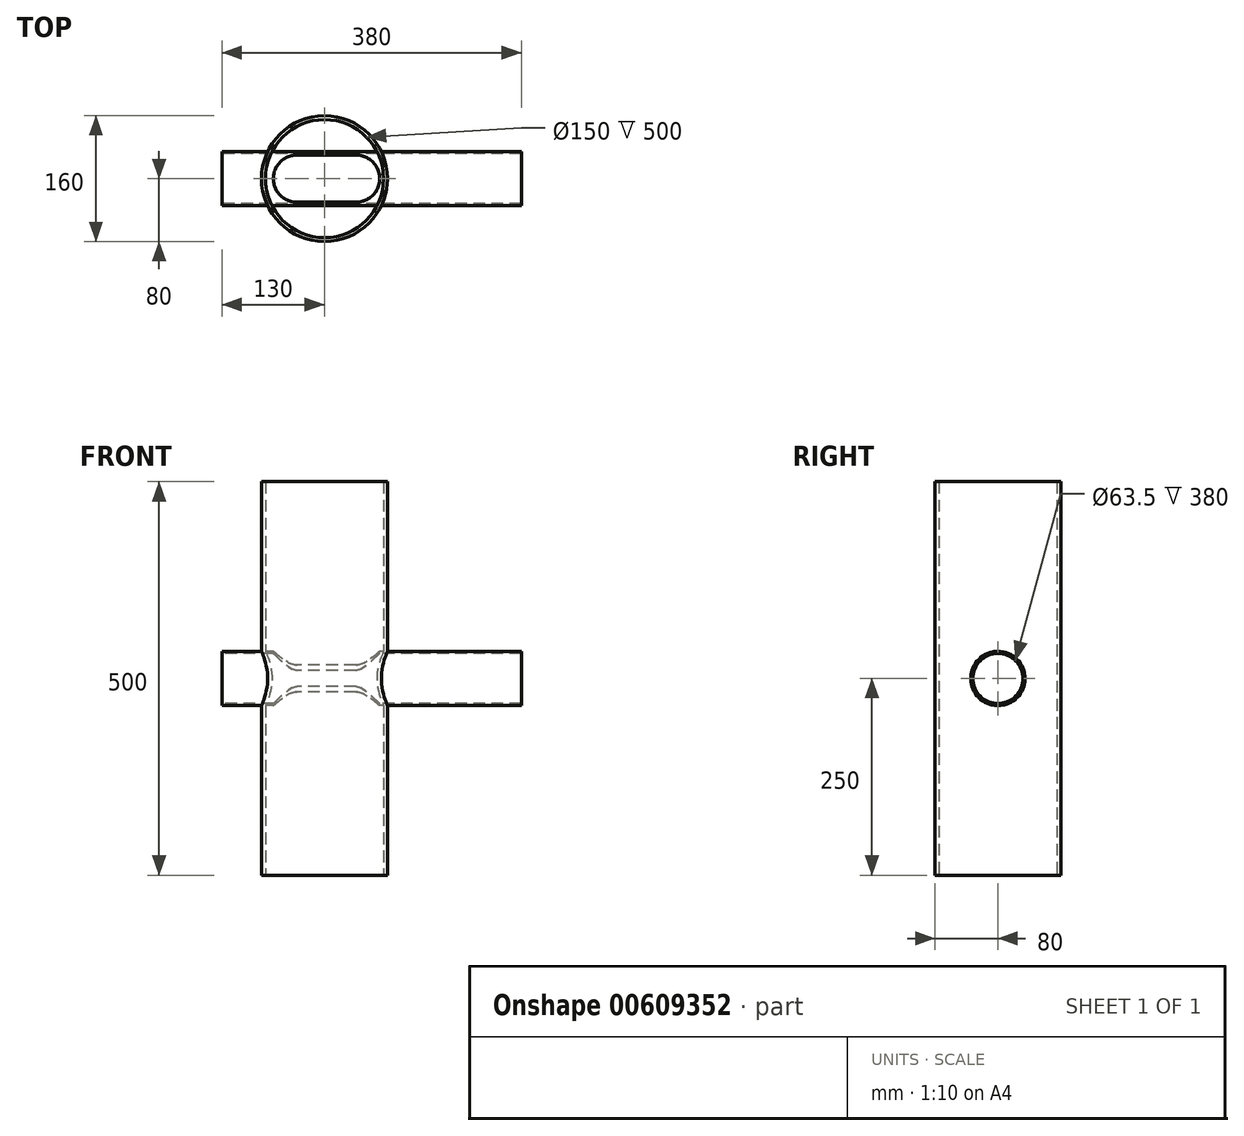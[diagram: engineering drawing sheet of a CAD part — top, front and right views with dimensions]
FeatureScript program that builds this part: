
annotation { "Feature Type Name" : "Feature", "Feature Type Description" : "" }
export const myFeature = defineFeature(function(context is Context, id is Id, definition is map)
    precondition{}
    {
        {
            var Q0;
            Q0=qCreatedBy(makeId("Top.planeOp"),FACE);
            var sketch = newSketch(context, id + "F0", { "sketchPlane" : qUnion([Q0])});
            skCircle(sketch, "E0", {"center": v(0, 0) * mm, "radius": 80 * mm});
            skCircle(sketch, "E1", {"center": v(0, 0) * mm, "radius": 75 * mm});
            skSolve(sketch);
        }
        {
            var Q0;
            Q0=makeQuery(id+"F0.imprint","IMPRINT",FACE,{"disambiguationData":[TD([[makeQuery(id+"F0.imprint","IMPRINT",EDGE,{"derivedFrom":sQuery(id+"F0.wireOp",EDGE,"E0")}),1.0]])]});
            extrude(context, id + "F1", {"entities" : qUnion([Q0]), "endBound" : BoundingType.SYMMETRIC, "depth" : 500 * mm, "offsetDistance" : 25 * mm});
        }
        {
            var Q0;
            Q0=qCreatedBy(makeId("Right.planeOp"),FACE);
            var sketch = newSketch(context, id + "F2", { "sketchPlane" : qUnion([Q0])});
            skCircle(sketch, "E2", {"center": v(0, 0) * mm, "radius": 31.75 * mm});
            skCircle(sketch, "E3", {"center": v(0, 0) * mm, "radius": 34.5 * mm});
            skSolve(sketch);
        }
        {
            var Q0;
            Q0=makeQuery(id+"F2.imprint","IMPRINT",FACE,{"disambiguationData":[TD([[makeQuery(id+"F2.imprint","IMPRINT",EDGE,{"derivedFrom":sQuery(id+"F2.wireOp",EDGE,"E2")}),-1.0]])]});
            extrude(context, id + "F3", {"entities" : qUnion([Q0]), "endBound" : BoundingType.SYMMETRIC, "depth" : 500 * mm, "offsetDistance" : 25 * mm});
        }
        {
            var Q0;
            Q0=qCreatedBy(makeId("Top.planeOp"),FACE);
            var sketch = newSketch(context, id + "F4", { "sketchPlane" : qUnion([Q0])});
            skCircle(sketch, "E4", {"center": v(0, 0) * mm, "radius": 75 * mm});
            skCircle(sketch, "E5", {"center": v(0, 0) * mm, "radius": 80 * mm});
            skSolve(sketch);
        }
        {
            var Q0;
            Q0=makeQuery(id+"F2.imprint","IMPRINT",FACE,{"disambiguationData":[TD([[makeQuery(id+"F2.imprint","IMPRINT",EDGE,{"derivedFrom":sQuery(id+"F2.wireOp",EDGE,"E2")}),1.0]])]});
            extrude(context, id + "F5", {"entities" : qUnion([Q0]), "operationType" : NewBodyOperationType.REMOVE, "endBound" : BoundingType.SYMMETRIC, "oppositeDirection" : true, "depth" : 500 * mm, "offsetDistance" : 25 * mm});
        }
        {
            var Q0;
            Q0=qCreatedBy(makeId("Top.planeOp"),FACE);
            var sketch = newSketch(context, id + "F6", { "sketchPlane" : qUnion([Q0])});
            skArc(sketch, "E6", {"start": v(-35.05, 19.92) * mm, "mid": v(-55.05, -0.08) * mm, "end": v(-35.05, -20.08) * mm});
            skArc(sketch, "E7", {"start": v(39.34, -20.08) * mm, "mid": v(59.34, -0.08) * mm, "end": v(39.34, 19.92) * mm});
            skLineSegment(sketch, "E8", {"start": v(-35.05, 19.92) * mm, "end": v(39.34, 19.92) * mm});
            skLineSegment(sketch, "E9", {"start": v(-35.05, -20.08) * mm, "end": v(39.34, -20.08) * mm});
            skSolve(sketch);
        }
        {
            var Q0;
            Q0=makeQuery(id+"F6.imprint","IMPRINT",FACE,{"disambiguationData":[TD([[makeQuery(id+"F6.imprint","IMPRINT",EDGE,{"derivedFrom":sQuery(id+"F6.wireOp",EDGE,"E6")}),1.0]])]});
            extrude(context, id + "F7", {"entities" : qUnion([Q0]), "endBound" : BoundingType.SYMMETRIC, "depth" : 100 * mm, "offsetDistance" : 25 * mm});
        }
        {
            var Q0;
            Q0=makeQuery(id+"F7.opExtrude","CAP_FACE",FACE,{"disambiguationData":[OSD([sQuery(id+"F6.wireOp",EDGE,"E6"),sQuery(id+"F6.wireOp",EDGE,"E7"),sQuery(id+"F6.wireOp",EDGE,"E8"),sQuery(id+"F6.wireOp",EDGE,"E9")])],"isStart":false});
            var sketch = newSketch(context, id + "F8", { "sketchPlane" : qUnion([Q0])});
            skLineSegment(sketch, "E10", {"start": v(-35.05, 19.92) * mm, "end": v(-35.05, -20.08) * mm});
            skLineSegment(sketch, "E11", {"start": v(39.34, 19.92) * mm, "end": v(39.34, -20.08) * mm});
            skSolve(sketch);
        }
        {
            var Q0;
            Q0=makeQuery(id+"F8.imprint","IMPRINT",FACE,{"disambiguationData":[TD([[makeQuery(id+"F8.imprint","IMPRINT",EDGE,{"derivedFrom":sQuery(id+"F8.wireOp",EDGE,"E10")}),1.0]])]});
            var sketch = newSketch(context, id + "F9", { "sketchPlane" : qUnion([Q0])});
            skArc(sketch, "E12", {"start": v(-35.02, 30) * mm, "mid": v(-65.02, 0) * mm, "end": v(-35.02, -30) * mm});
            skArc(sketch, "E13", {"start": v(39.98, -30) * mm, "mid": v(69.98, 0) * mm, "end": v(39.98, 30) * mm});
            skLineSegment(sketch, "E14", {"start": v(-35.02, 30) * mm, "end": v(39.98, 30) * mm});
            skLineSegment(sketch, "E15", {"start": v(39.98, -30) * mm, "end": v(-35.02, -30) * mm});
            skSolve(sketch);
        }
        {
            var Q0;
            Q0 = qSketchRegion(id + "F9", true);
            extrude(context, id + "F10", {"entities" : qUnion([Q0]), "operationType" : NewBodyOperationType.REMOVE, "oppositeDirection" : true, "depth" : 200 * mm, "offsetDistance" : 25 * mm});
        }
        {
            var Q0;
            Q0=qCreatedBy(makeId("Top.planeOp"),FACE);
            var sketch = newSketch(context, id + "F11", { "sketchPlane" : qUnion([Q0])});
            skSolve(sketch);
        }
        {
            var Q0;
            Q0 = qSketchRegion(id + "F11", true);
            var Q1;
            Q1=makeQuery(id+"F0.imprint","IMPRINT",FACE,{"disambiguationData":[TD([[makeQuery(id+"F0.imprint","IMPRINT",EDGE,{"derivedFrom":sQuery(id+"F0.wireOp",EDGE,"E0")}),1.0]])]});
            extrude(context, id + "F12", {"entities" : qUnion([Q0, Q1]), "operationType" : NewBodyOperationType.ADD, "endBound" : BoundingType.SYMMETRIC, "depth" : 500 * mm, "offsetDistance" : 25 * mm});
        }
        {
            var Q0;
            Q0=qCreatedBy(makeId("Right.planeOp"),FACE);
            var sketch = newSketch(context, id + "F13", { "sketchPlane" : qUnion([Q0])});
            skCircle(sketch, "E16", {"center": v(0, 0) * mm, "radius": 31.75 * mm});
            skSolve(sketch);
        }
        {
            var Q0;
            Q0 = qSketchRegion(id + "F13", true);
            var Q1;
            Q1=makeQuery(id+"F2.imprint","IMPRINT",FACE,{"disambiguationData":[TD([[makeQuery(id+"F2.imprint","IMPRINT",EDGE,{"derivedFrom":sQuery(id+"F2.wireOp",EDGE,"E2")}),1.0]])]});
            extrude(context, id + "F14", {"entities" : qUnion([Q0, Q1]), "operationType" : NewBodyOperationType.REMOVE, "endBound" : BoundingType.SYMMETRIC, "oppositeDirection" : true, "depth" : 500 * mm, "offsetDistance" : 25 * mm});
        }
        {
            var Q0;
            Q0=makeQuery(id+"F3.opExtrude","CAP_FACE",FACE,{"disambiguationData":[OSD([sQuery(id+"F2.wireOp",EDGE,"E2"),sQuery(id+"F2.wireOp",EDGE,"E3")])],"isStart":true});
            extrude(context, id + "F15", {"entities" : qUnion([Q0]), "operationType" : NewBodyOperationType.REMOVE, "oppositeDirection" : true, "depth" : 160 * mm, "offsetDistance" : 25 * mm});
        }
        {
            var Q0;
            Q0=makeQuery(id+"F15.boolean.opBoolean","COPY",FACE,{"derivedFrom":makeQuery(id+"F15.opExtrude","CAP_FACE",FACE,{"disambiguationData":[OSD([sQuery(id+"F2.wireOp",EDGE,"E2"),sQuery(id+"F2.wireOp",EDGE,"E3")])],"isStart":false})});
            extrude(context, id + "F16", {"entities" : qUnion([Q0]), "operationType" : NewBodyOperationType.ADD, "depth" : 40 * mm, "offsetDistance" : 25 * mm});
        }
    });
